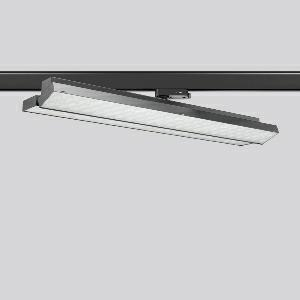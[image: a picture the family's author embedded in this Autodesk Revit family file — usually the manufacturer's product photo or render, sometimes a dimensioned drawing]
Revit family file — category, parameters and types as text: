
# Revit family: tx-move_742162_003_1_76_0629
name_source: partatom
category: Lighting Fixtures
units: mm (PartAtom-declared; Revit-internal decimal feet)

## family parameters
Cut with Voids When Loaded = No
Host = Face
Light Source = No
Part Type = Normal
Room Calculation Point = No
Round Connector Dimension = Use Diameter
Shared = No

## types (1)
- MultiLumen 1 (1 x LED Modul 840, 3150 lm, 4000)
    Apparent Load = 41 VA
    CIE Flux Codes = 77 96 99 100 100
    Color Rendering = 80
    Color Temperature = 4000
    Default Elevation = 1800 mm
    Description = Series: TX-MOVE
Multifunctional surface-mounted spotlight for area lighting. Very flat design. Housing: sheet steel, powder-coated. Rotation range: 356°. Swivel range: 90°. Consistent alignment possible with visible tilt scale. High-efficiency LED units with optimum light control thanks to clear plastic (PC) lens optics. Spezielle Mikrostrukturen reduzieren Gelbsaum. Symmetrical light distribution. With adapter for RZB 3-circuit DALI tracks. Suitable for Track on ceiling. MultiLumen: Luminous flux adjustable in 3 steps. Factory setting is the highest luminous flux. Environmentally friendly and resource-saving due to replaceable and recyclable components. 
Colour: deep black, matt (RAL 9005)
Length: 570 mm
Width: 119 mm
Height: 88 mm
Lamp: LED
Socket: without socket
Colour temperature: 4000K
Colour rendering index (CRI): 80
System power: 41 W
Rated luminous flux: 6300 lm
Luminous efficiency: 154 lm/W
System power 2: 57 W
Rated luminous flux 2: 8550 lm
Luminous efficiency 2: 150 lm/W
System power 3: 73 W
Rated luminous flux 3: 10400 lm
Luminous efficiency 3: 142 lm/W
Control gear: Dimmable EVG, DALI
Protection class: I
Type of protection: IP 20
    Height = 75 mm
    Lamp = 1 x LED Modul 840
    Lamp Light Flux = 3150 lm
    Lamp count = 1
    Length = 569 mm
    Lifetime = 50000 h
    Luminous efficacy = 154 lm/W
    Manufacturer = RZB
    ModVariant = No
    Model = 742162.003.1.76
    Mounting Place = Ceiling
    Mounting Type = Surface mounted
    Number of Poles = 1
    OnlyDefault = Yes
    Power Factor = 1
    Product Name = TX-MOVE
    Product group = Track mounted projectors
    ProductGroupID = 301
    Protection Class = Protection class I
    Protection Degree = IP 20
    RLX_Detail_Level = 1
    RLX_Emergency_Light_Flux = 0 lm
    RLX_Emergency_Type = 0
    RLX_Emergency_Type_DB = No
    RlxData = <blob elided: 36709 chars, md5=f47f438f>
    Socket = socket
    Standby Power = 0 W
    System Light Flux = 6300 lm
    System Power = 41 W
    Type Comments = MultiLumen 1
    Type Image = 742162.003.jpg
    URL = http://relux.com
    VarID = multilumen_1
    Voltage = 0 V
    Weight = 0.00 kg
    Width = 119 mm

## geometry (parser evidence)
native form markers: Blend x4, Sweep x15
no freeform markers — native parametric forms only
